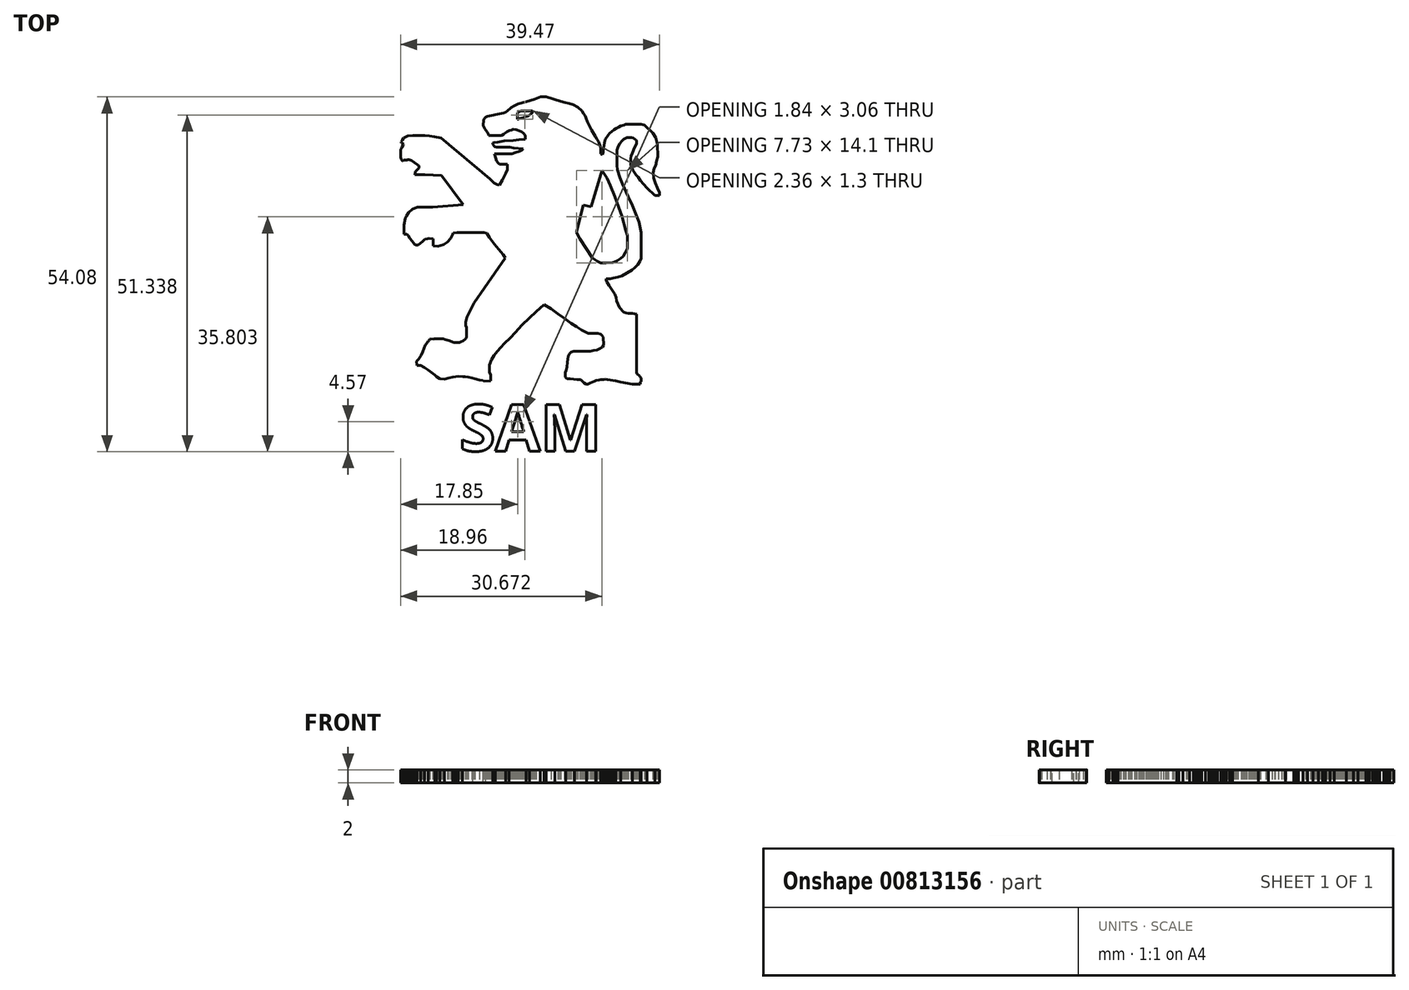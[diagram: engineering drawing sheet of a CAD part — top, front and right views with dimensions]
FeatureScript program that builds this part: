
annotation { "Feature Type Name" : "Feature", "Feature Type Description" : "" }
export const myFeature = defineFeature(function(context is Context, id is Id, definition is map)
    precondition{}
    {
        {
            var Q0;
            Q0=qCreatedBy(makeId("Top.planeOp"),FACE);
            var sketch = newSketch(context, id + "F0", { "sketchPlane" : qUnion([Q0])});
            skLineSegment(sketch, "E0", {"start": v(13.97, 0.9) * mm, "end": v(13.97, 1.77) * mm});
            skLineSegment(sketch, "E1", {"start": v(13.97, 1.77) * mm, "end": v(13.78, 2.26) * mm});
            skLineSegment(sketch, "E2", {"start": v(13.78, 2.26) * mm, "end": v(13.78, 3.3) * mm});
            skLineSegment(sketch, "E3", {"start": v(13.78, 3.3) * mm, "end": v(14.1, 4.13) * mm});
            skLineSegment(sketch, "E4", {"start": v(14.1, 4.13) * mm, "end": v(14.5, 4.8) * mm});
            skLineSegment(sketch, "E5", {"start": v(14.5, 4.8) * mm, "end": v(15, 5.39) * mm});
            skLineSegment(sketch, "E6", {"start": v(15, 5.39) * mm, "end": v(15.48, 5.98) * mm});
            skLineSegment(sketch, "E7", {"start": v(15.48, 5.98) * mm, "end": v(16.06, 6.6) * mm});
            skLineSegment(sketch, "E8", {"start": v(16.06, 6.6) * mm, "end": v(16.94, 7.44) * mm});
            skLineSegment(sketch, "E9", {"start": v(16.94, 7.44) * mm, "end": v(17.73, 8.26) * mm});
            skLineSegment(sketch, "E10", {"start": v(17.73, 8.26) * mm, "end": v(18.78, 9.4) * mm});
            skLineSegment(sketch, "E11", {"start": v(18.78, 9.4) * mm, "end": v(19.9, 10.48) * mm});
            skLineSegment(sketch, "E12", {"start": v(19.9, 10.48) * mm, "end": v(20.9, 11.46) * mm});
            skLineSegment(sketch, "E13", {"start": v(20.9, 11.46) * mm, "end": v(22.1, 12.53) * mm});
            skLineSegment(sketch, "E14", {"start": v(22.1, 12.53) * mm, "end": v(23.17, 11.89) * mm});
            skLineSegment(sketch, "E15", {"start": v(23.17, 11.89) * mm, "end": v(24.23, 11.11) * mm});
            skLineSegment(sketch, "E16", {"start": v(24.23, 11.11) * mm, "end": v(25.22, 10.45) * mm});
            skLineSegment(sketch, "E17", {"start": v(25.22, 10.45) * mm, "end": v(26.25, 9.7) * mm});
            skLineSegment(sketch, "E18", {"start": v(26.25, 9.7) * mm, "end": v(27.06, 9.18) * mm});
            skLineSegment(sketch, "E19", {"start": v(27.06, 9.18) * mm, "end": v(27.84, 8.67) * mm});
            skLineSegment(sketch, "E20", {"start": v(27.84, 8.67) * mm, "end": v(28.85, 8.16) * mm});
            skLineSegment(sketch, "E21", {"start": v(28.85, 8.16) * mm, "end": v(30.3, 8.16) * mm});
            skLineSegment(sketch, "E22", {"start": v(30.3, 8.16) * mm, "end": v(30.76, 8) * mm});
            skLineSegment(sketch, "E23", {"start": v(30.76, 8) * mm, "end": v(30.95, 7.82) * mm});
            skLineSegment(sketch, "E24", {"start": v(30.95, 7.82) * mm, "end": v(31.1, 7.55) * mm});
            skLineSegment(sketch, "E25", {"start": v(31.1, 7.55) * mm, "end": v(31.17, 6.37) * mm});
            skLineSegment(sketch, "E26", {"start": v(31.17, 6.37) * mm, "end": v(30.99, 6.03) * mm});
            skLineSegment(sketch, "E27", {"start": v(30.99, 6.03) * mm, "end": v(30.55, 5.77) * mm});
            skLineSegment(sketch, "E28", {"start": v(30.55, 5.77) * mm, "end": v(30.16, 5.62) * mm});
            skLineSegment(sketch, "E29", {"start": v(30.16, 5.62) * mm, "end": v(29.68, 5.5) * mm});
            skLineSegment(sketch, "E30", {"start": v(29.68, 5.5) * mm, "end": v(29.13, 5.42) * mm});
            skLineSegment(sketch, "E31", {"start": v(29.13, 5.42) * mm, "end": v(26.64, 5.42) * mm});
            skLineSegment(sketch, "E32", {"start": v(26.64, 5.42) * mm, "end": v(26.27, 5.28) * mm});
            skLineSegment(sketch, "E33", {"start": v(26.27, 5.28) * mm, "end": v(26, 5.01) * mm});
            skLineSegment(sketch, "E34", {"start": v(26, 5.01) * mm, "end": v(25.83, 4.63) * mm});
            skLineSegment(sketch, "E35", {"start": v(25.83, 4.63) * mm, "end": v(25.7, 3.74) * mm});
            skLineSegment(sketch, "E36", {"start": v(25.7, 3.74) * mm, "end": v(25.59, 3.02) * mm});
            skLineSegment(sketch, "E37", {"start": v(25.59, 3.02) * mm, "end": v(25.45, 2.5) * mm});
            skLineSegment(sketch, "E38", {"start": v(25.45, 2.5) * mm, "end": v(25.34, 2.18) * mm});
            skLineSegment(sketch, "E39", {"start": v(25.34, 2.18) * mm, "end": v(25.34, 1.47) * mm});
            skLineSegment(sketch, "E40", {"start": v(25.34, 1.47) * mm, "end": v(25.6, 1.23) * mm});
            skLineSegment(sketch, "E41", {"start": v(25.6, 1.23) * mm, "end": v(26.1, 1.23) * mm});
            skLineSegment(sketch, "E42", {"start": v(26.1, 1.23) * mm, "end": v(26.61, 1.15) * mm});
            skLineSegment(sketch, "E43", {"start": v(26.61, 1.15) * mm, "end": v(27.13, 1.07) * mm});
            skLineSegment(sketch, "E44", {"start": v(27.13, 1.07) * mm, "end": v(27.68, 1.07) * mm});
            skLineSegment(sketch, "E45", {"start": v(27.68, 1.07) * mm, "end": v(27.95, 0.82) * mm});
            skLineSegment(sketch, "E46", {"start": v(27.95, 0.82) * mm, "end": v(28.2, 0.58) * mm});
            skLineSegment(sketch, "E47", {"start": v(28.2, 0.58) * mm, "end": v(28.54, 0.4) * mm});
            skLineSegment(sketch, "E48", {"start": v(28.54, 0.4) * mm, "end": v(28.79, 0.4) * mm});
            skLineSegment(sketch, "E49", {"start": v(28.79, 0.4) * mm, "end": v(29.18, 0.58) * mm});
            skLineSegment(sketch, "E50", {"start": v(29.18, 0.58) * mm, "end": v(29.45, 0.7) * mm});
            skLineSegment(sketch, "E51", {"start": v(29.45, 0.7) * mm, "end": v(29.78, 0.82) * mm});
            skLineSegment(sketch, "E52", {"start": v(29.78, 0.82) * mm, "end": v(30.07, 0.95) * mm});
            skLineSegment(sketch, "E53", {"start": v(30.07, 0.95) * mm, "end": v(30.46, 1.03) * mm});
            skLineSegment(sketch, "E54", {"start": v(30.46, 1.03) * mm, "end": v(30.78, 1.1) * mm});
            skLineSegment(sketch, "E55", {"start": v(30.78, 1.1) * mm, "end": v(31.2, 1.1) * mm});
            skLineSegment(sketch, "E56", {"start": v(31.2, 1.1) * mm, "end": v(31.46, 1.15) * mm});
            skLineSegment(sketch, "E57", {"start": v(31.46, 1.15) * mm, "end": v(31.77, 1.08) * mm});
            skLineSegment(sketch, "E58", {"start": v(31.77, 1.08) * mm, "end": v(32.19, 1.02) * mm});
            skLineSegment(sketch, "E59", {"start": v(32.19, 1.02) * mm, "end": v(32.57, 0.95) * mm});
            skLineSegment(sketch, "E60", {"start": v(32.57, 0.95) * mm, "end": v(33.05, 0.88) * mm});
            skLineSegment(sketch, "E61", {"start": v(33.05, 0.88) * mm, "end": v(33.8, 0.71) * mm});
            skLineSegment(sketch, "E62", {"start": v(33.8, 0.71) * mm, "end": v(35.55, 0.37) * mm});
            skLineSegment(sketch, "E63", {"start": v(35.55, 0.37) * mm, "end": v(36.8, 0.37) * mm});
            skLineSegment(sketch, "E64", {"start": v(36.8, 0.37) * mm, "end": v(36.8, 0.75) * mm});
            skLineSegment(sketch, "E65", {"start": v(36.8, 0.75) * mm, "end": v(36.88, 0.75) * mm});
            skLineSegment(sketch, "E66", {"start": v(36.88, 0.75) * mm, "end": v(36.88, 1.34) * mm});
            skLineSegment(sketch, "E67", {"start": v(36.88, 1.34) * mm, "end": v(36.7, 1.52) * mm});
            skLineSegment(sketch, "E68", {"start": v(36.7, 1.52) * mm, "end": v(36.66, 1.64) * mm});
            skLineSegment(sketch, "E69", {"start": v(36.66, 1.64) * mm, "end": v(36.28, 2) * mm});
            skLineSegment(sketch, "E70", {"start": v(36.28, 2) * mm, "end": v(36.22, 2.16) * mm});
            skLineSegment(sketch, "E71", {"start": v(36.22, 2.16) * mm, "end": v(36.22, 11.05) * mm});
            skLineSegment(sketch, "E72", {"start": v(36.22, 11.05) * mm, "end": v(35.57, 11.18) * mm});
            skLineSegment(sketch, "E73", {"start": v(35.57, 11.18) * mm, "end": v(34.95, 11.18) * mm});
            skLineSegment(sketch, "E74", {"start": v(34.95, 11.18) * mm, "end": v(34.6, 11.25) * mm});
            skLineSegment(sketch, "E75", {"start": v(34.6, 11.25) * mm, "end": v(34.26, 11.4) * mm});
            skLineSegment(sketch, "E76", {"start": v(34.26, 11.4) * mm, "end": v(33.93, 11.72) * mm});
            skLineSegment(sketch, "E77", {"start": v(33.93, 11.72) * mm, "end": v(33.59, 12.05) * mm});
            skLineSegment(sketch, "E78", {"start": v(33.59, 12.05) * mm, "end": v(33.4, 12.53) * mm});
            skLineSegment(sketch, "E79", {"start": v(33.4, 12.53) * mm, "end": v(33.2, 13.07) * mm});
            skLineSegment(sketch, "E80", {"start": v(33.2, 13.07) * mm, "end": v(33.07, 13.59) * mm});
            skLineSegment(sketch, "E81", {"start": v(33.07, 13.59) * mm, "end": v(32.88, 14.08) * mm});
            skLineSegment(sketch, "E82", {"start": v(32.88, 14.08) * mm, "end": v(32.65, 14.48) * mm});
            skLineSegment(sketch, "E83", {"start": v(32.65, 14.48) * mm, "end": v(32.38, 14.9) * mm});
            skLineSegment(sketch, "E84", {"start": v(32.38, 14.9) * mm, "end": v(32, 15.46) * mm});
            skLineSegment(sketch, "E85", {"start": v(32, 15.46) * mm, "end": v(31.7, 15.95) * mm});
            skLineSegment(sketch, "E86", {"start": v(31.7, 15.95) * mm, "end": v(31.56, 16.28) * mm});
            skLineSegment(sketch, "E87", {"start": v(31.56, 16.28) * mm, "end": v(31.6, 16.45) * mm});
            skLineSegment(sketch, "E88", {"start": v(31.6, 16.45) * mm, "end": v(32.18, 16.45) * mm});
            skLineSegment(sketch, "E89", {"start": v(32.18, 16.45) * mm, "end": v(32.7, 16.57) * mm});
            skLineSegment(sketch, "E90", {"start": v(32.7, 16.57) * mm, "end": v(33.34, 16.74) * mm});
            skLineSegment(sketch, "E91", {"start": v(33.34, 16.74) * mm, "end": v(33.96, 16.92) * mm});
            skLineSegment(sketch, "E92", {"start": v(33.96, 16.92) * mm, "end": v(34.77, 17.32) * mm});
            skLineSegment(sketch, "E93", {"start": v(34.77, 17.32) * mm, "end": v(35.5, 17.8) * mm});
            skLineSegment(sketch, "E94", {"start": v(35.5, 17.8) * mm, "end": v(35.97, 18.18) * mm});
            skLineSegment(sketch, "E95", {"start": v(35.97, 18.18) * mm, "end": v(36.4, 18.63) * mm});
            skLineSegment(sketch, "E96", {"start": v(36.4, 18.63) * mm, "end": v(36.73, 19.12) * mm});
            skLineSegment(sketch, "E97", {"start": v(36.73, 19.12) * mm, "end": v(36.88, 19.57) * mm});
            skLineSegment(sketch, "E98", {"start": v(36.88, 19.57) * mm, "end": v(36.88, 23.54) * mm});
            skLineSegment(sketch, "E99", {"start": v(36.88, 23.54) * mm, "end": v(36.56, 25.08) * mm});
            skPoint(sketch, "E99.endSnap0", {"position": v(36.56, 18.87) * mm});
            skLineSegment(sketch, "E100", {"start": v(36.56, 25.08) * mm, "end": v(36.04, 26.42) * mm});
            skLineSegment(sketch, "E101", {"start": v(36.04, 26.42) * mm, "end": v(35.56, 27.66) * mm});
            skLineSegment(sketch, "E102", {"start": v(35.56, 27.66) * mm, "end": v(34.95, 28.94) * mm});
            skLineSegment(sketch, "E103", {"start": v(34.95, 28.94) * mm, "end": v(34.56, 29.8) * mm});
            skLineSegment(sketch, "E104", {"start": v(34.56, 29.8) * mm, "end": v(34.05, 30.91) * mm});
            skLineSegment(sketch, "E105", {"start": v(34.05, 30.91) * mm, "end": v(33.67, 31.9) * mm});
            skLineSegment(sketch, "E106", {"start": v(33.67, 31.9) * mm, "end": v(33.32, 33.1) * mm});
            skLineSegment(sketch, "E107", {"start": v(33.32, 33.1) * mm, "end": v(33.23, 33.72) * mm});
            skLineSegment(sketch, "E108", {"start": v(33.23, 33.72) * mm, "end": v(33.23, 36.07) * mm});
            skLineSegment(sketch, "E109", {"start": v(33.23, 36.07) * mm, "end": v(33.42, 36.63) * mm});
            skLineSegment(sketch, "E110", {"start": v(33.42, 36.63) * mm, "end": v(33.67, 37.12) * mm});
            skLineSegment(sketch, "E111", {"start": v(33.67, 37.12) * mm, "end": v(33.96, 37.49) * mm});
            skLineSegment(sketch, "E112", {"start": v(33.96, 37.49) * mm, "end": v(34.22, 37.75) * mm});
            skLineSegment(sketch, "E113", {"start": v(34.22, 37.75) * mm, "end": v(34.47, 37.87) * mm});
            skLineSegment(sketch, "E114", {"start": v(34.47, 37.87) * mm, "end": v(34.73, 37.98) * mm});
            skLineSegment(sketch, "E115", {"start": v(34.73, 37.98) * mm, "end": v(35.44, 37.98) * mm});
            skLineSegment(sketch, "E116", {"start": v(35.44, 37.98) * mm, "end": v(35.7, 37.9) * mm});
            skLineSegment(sketch, "E117", {"start": v(35.7, 37.9) * mm, "end": v(35.97, 37.76) * mm});
            skLineSegment(sketch, "E118", {"start": v(35.97, 37.76) * mm, "end": v(36.12, 37.6) * mm});
            skLineSegment(sketch, "E119", {"start": v(36.12, 37.6) * mm, "end": v(36.22, 37.46) * mm});
            skLineSegment(sketch, "E120", {"start": v(36.22, 37.46) * mm, "end": v(36.22, 37.03) * mm});
            skLineSegment(sketch, "E121", {"start": v(36.22, 37.03) * mm, "end": v(36.1, 36.8) * mm});
            skLineSegment(sketch, "E122", {"start": v(36.1, 36.8) * mm, "end": v(35.92, 36.44) * mm});
            skLineSegment(sketch, "E123", {"start": v(35.92, 36.44) * mm, "end": v(35.55, 35.66) * mm});
            skLineSegment(sketch, "E124", {"start": v(35.55, 35.66) * mm, "end": v(35.4, 35.18) * mm});
            skLineSegment(sketch, "E125", {"start": v(35.4, 35.18) * mm, "end": v(35.32, 34.8) * mm});
            skLineSegment(sketch, "E126", {"start": v(35.32, 34.8) * mm, "end": v(35.32, 33.86) * mm});
            skLineSegment(sketch, "E127", {"start": v(35.32, 33.86) * mm, "end": v(35.45, 33.51) * mm});
            skLineSegment(sketch, "E128", {"start": v(35.45, 33.51) * mm, "end": v(35.66, 33.06) * mm});
            skLineSegment(sketch, "E129", {"start": v(35.66, 33.06) * mm, "end": v(35.9, 32.68) * mm});
            skLineSegment(sketch, "E130", {"start": v(35.9, 32.68) * mm, "end": v(36.17, 32.25) * mm});
            skLineSegment(sketch, "E131", {"start": v(36.17, 32.25) * mm, "end": v(36.45, 31.93) * mm});
            skLineSegment(sketch, "E132", {"start": v(36.45, 31.93) * mm, "end": v(36.79, 31.47) * mm});
            skLineSegment(sketch, "E133", {"start": v(36.79, 31.47) * mm, "end": v(37.29, 30.9) * mm});
            skLineSegment(sketch, "E134", {"start": v(37.29, 30.9) * mm, "end": v(37.8, 30.3) * mm});
            skLineSegment(sketch, "E135", {"start": v(37.8, 30.3) * mm, "end": v(38.48, 29.64) * mm});
            skLineSegment(sketch, "E136", {"start": v(38.48, 29.64) * mm, "end": v(38.98, 29.16) * mm});
            skLineSegment(sketch, "E137", {"start": v(38.98, 29.16) * mm, "end": v(39.73, 29.16) * mm});
            skLineSegment(sketch, "E138", {"start": v(39.73, 29.16) * mm, "end": v(39.73, 29.6) * mm});
            skLineSegment(sketch, "E139", {"start": v(39.73, 29.6) * mm, "end": v(39.38, 30.31) * mm});
            skLineSegment(sketch, "E140", {"start": v(39.38, 30.31) * mm, "end": v(39.09, 31.04) * mm});
            skLineSegment(sketch, "E141", {"start": v(39.09, 31.04) * mm, "end": v(38.84, 31.82) * mm});
            skLineSegment(sketch, "E142", {"start": v(38.84, 31.82) * mm, "end": v(38.78, 32.67) * mm});
            skLineSegment(sketch, "E143", {"start": v(38.78, 32.67) * mm, "end": v(38.9, 33.28) * mm});
            skLineSegment(sketch, "E144", {"start": v(38.9, 33.28) * mm, "end": v(39.14, 33.76) * mm});
            skLineSegment(sketch, "E145", {"start": v(39.14, 33.76) * mm, "end": v(39.27, 34.44) * mm});
            skLineSegment(sketch, "E146", {"start": v(39.27, 34.44) * mm, "end": v(39.45, 35.1) * mm});
            skLineSegment(sketch, "E147", {"start": v(39.45, 35.1) * mm, "end": v(39.36, 36.94) * mm});
            skPoint(sketch, "E147.endSnap0", {"position": v(39.36, 34.76) * mm});
            skLineSegment(sketch, "E148", {"start": v(39.36, 36.94) * mm, "end": v(39.14, 37.98) * mm});
            skLineSegment(sketch, "E149", {"start": v(39.14, 37.98) * mm, "end": v(38.7, 38.68) * mm});
            skLineSegment(sketch, "E150", {"start": v(38.7, 38.68) * mm, "end": v(37.8, 39.55) * mm});
            skLineSegment(sketch, "E151", {"start": v(37.8, 39.55) * mm, "end": v(37.42, 39.9) * mm});
            skLineSegment(sketch, "E152", {"start": v(37.42, 39.9) * mm, "end": v(36.88, 40.01) * mm});
            skLineSegment(sketch, "E153", {"start": v(36.88, 40.01) * mm, "end": v(34.56, 40.01) * mm});
            skLineSegment(sketch, "E154", {"start": v(34.56, 40.01) * mm, "end": v(34.3, 39.9) * mm});
            skLineSegment(sketch, "E155", {"start": v(34.3, 39.9) * mm, "end": v(33.8, 39.79) * mm});
            skLineSegment(sketch, "E156", {"start": v(33.8, 39.79) * mm, "end": v(33.48, 39.6) * mm});
            skLineSegment(sketch, "E157", {"start": v(33.48, 39.6) * mm, "end": v(33.12, 39.4) * mm});
            skLineSegment(sketch, "E158", {"start": v(33.12, 39.4) * mm, "end": v(32.8, 39.19) * mm});
            skLineSegment(sketch, "E159", {"start": v(32.8, 39.19) * mm, "end": v(32.5, 38.95) * mm});
            skLineSegment(sketch, "E160", {"start": v(32.5, 38.95) * mm, "end": v(32.1, 38.6) * mm});
            skLineSegment(sketch, "E161", {"start": v(32.1, 38.6) * mm, "end": v(31.9, 38.35) * mm});
            skLineSegment(sketch, "E162", {"start": v(31.9, 38.35) * mm, "end": v(31.72, 38.09) * mm});
            skLineSegment(sketch, "E163", {"start": v(31.72, 38.09) * mm, "end": v(31.47, 37.7) * mm});
            skLineSegment(sketch, "E164", {"start": v(31.47, 37.7) * mm, "end": v(31.34, 37.23) * mm});
            skLineSegment(sketch, "E165", {"start": v(31.34, 37.23) * mm, "end": v(31.25, 36.8) * mm});
            skLineSegment(sketch, "E166", {"start": v(31.25, 36.8) * mm, "end": v(31.18, 36.42) * mm});
            skLineSegment(sketch, "E167", {"start": v(31.18, 36.42) * mm, "end": v(31.12, 35.86) * mm});
            skLineSegment(sketch, "E168", {"start": v(31.12, 35.86) * mm, "end": v(31.05, 35.5) * mm});
            skLineSegment(sketch, "E169", {"start": v(31.05, 35.5) * mm, "end": v(31, 35.38) * mm});
            skLineSegment(sketch, "E170", {"start": v(31, 35.38) * mm, "end": v(30.77, 35.53) * mm});
            skLineSegment(sketch, "E171", {"start": v(30.77, 35.53) * mm, "end": v(30.77, 36.26) * mm});
            skLineSegment(sketch, "E172", {"start": v(30.77, 36.26) * mm, "end": v(30.66, 36.66) * mm});
            skLineSegment(sketch, "E173", {"start": v(30.66, 36.66) * mm, "end": v(30.4, 37.32) * mm});
            skLineSegment(sketch, "E174", {"start": v(30.4, 37.32) * mm, "end": v(30.16, 37.7) * mm});
            skLineSegment(sketch, "E175", {"start": v(30.16, 37.7) * mm, "end": v(29.9, 38.19) * mm});
            skLineSegment(sketch, "E176", {"start": v(29.9, 38.19) * mm, "end": v(29.57, 38.72) * mm});
            skLineSegment(sketch, "E177", {"start": v(29.57, 38.72) * mm, "end": v(29.32, 39.1) * mm});
            skLineSegment(sketch, "E178", {"start": v(29.32, 39.1) * mm, "end": v(29.15, 39.48) * mm});
            skLineSegment(sketch, "E179", {"start": v(29.15, 39.48) * mm, "end": v(28.93, 39.97) * mm});
            skLineSegment(sketch, "E180", {"start": v(28.93, 39.97) * mm, "end": v(28.72, 40.42) * mm});
            skLineSegment(sketch, "E181", {"start": v(28.72, 40.42) * mm, "end": v(28.54, 40.9) * mm});
            skLineSegment(sketch, "E182", {"start": v(28.54, 40.9) * mm, "end": v(28.38, 41.3) * mm});
            skLineSegment(sketch, "E183", {"start": v(28.38, 41.3) * mm, "end": v(28.17, 41.6) * mm});
            skLineSegment(sketch, "E184", {"start": v(28.17, 41.6) * mm, "end": v(27.9, 42.03) * mm});
            skLineSegment(sketch, "E185", {"start": v(27.9, 42.03) * mm, "end": v(27.28, 42.62) * mm});
            skLineSegment(sketch, "E186", {"start": v(27.28, 42.62) * mm, "end": v(26.96, 42.78) * mm});
            skLineSegment(sketch, "E187", {"start": v(26.96, 42.78) * mm, "end": v(26.57, 42.98) * mm});
            skLineSegment(sketch, "E188", {"start": v(26.57, 42.98) * mm, "end": v(25.92, 43.2) * mm});
            skLineSegment(sketch, "E189", {"start": v(25.92, 43.2) * mm, "end": v(25.34, 43.32) * mm});
            skLineSegment(sketch, "E190", {"start": v(25.34, 43.32) * mm, "end": v(24.65, 43.5) * mm});
            skLineSegment(sketch, "E191", {"start": v(24.65, 43.5) * mm, "end": v(22.4, 44.18) * mm});
            skLineSegment(sketch, "E192", {"start": v(22.4, 44.18) * mm, "end": v(21.62, 44.18) * mm});
            skLineSegment(sketch, "E193", {"start": v(21.62, 44.18) * mm, "end": v(20.63, 43.8) * mm});
            skLineSegment(sketch, "E194", {"start": v(20.63, 43.8) * mm, "end": v(19.41, 43.47) * mm});
            skLineSegment(sketch, "E195", {"start": v(19.41, 43.47) * mm, "end": v(18.2, 43.12) * mm});
            skLineSegment(sketch, "E196", {"start": v(18.2, 43.12) * mm, "end": v(17.53, 42.81) * mm});
            skLineSegment(sketch, "E197", {"start": v(17.53, 42.81) * mm, "end": v(17.1, 42.55) * mm});
            skLineSegment(sketch, "E198", {"start": v(17.1, 42.55) * mm, "end": v(16.76, 42.25) * mm});
            skLineSegment(sketch, "E199", {"start": v(16.76, 42.25) * mm, "end": v(16.47, 42) * mm});
            skLineSegment(sketch, "E200", {"start": v(16.47, 42) * mm, "end": v(16.3, 41.88) * mm});
            skLineSegment(sketch, "E201", {"start": v(16.3, 41.88) * mm, "end": v(15.98, 41.76) * mm});
            skLineSegment(sketch, "E202", {"start": v(15.98, 41.76) * mm, "end": v(15.63, 41.67) * mm});
            skLineSegment(sketch, "E203", {"start": v(15.63, 41.67) * mm, "end": v(13.48, 41.23) * mm});
            skLineSegment(sketch, "E204", {"start": v(13.48, 41.23) * mm, "end": v(13.22, 41.1) * mm});
            skLineSegment(sketch, "E205", {"start": v(13.22, 41.1) * mm, "end": v(13.02, 40.88) * mm});
            skLineSegment(sketch, "E206", {"start": v(13.02, 40.88) * mm, "end": v(12.91, 40.67) * mm});
            skLineSegment(sketch, "E207", {"start": v(12.91, 40.67) * mm, "end": v(12.86, 39.83) * mm});
            skLineSegment(sketch, "E208", {"start": v(12.86, 39.83) * mm, "end": v(12.97, 39.58) * mm});
            skLineSegment(sketch, "E209", {"start": v(12.97, 39.58) * mm, "end": v(13.08, 39.35) * mm});
            skLineSegment(sketch, "E210", {"start": v(13.08, 39.35) * mm, "end": v(13.24, 39.13) * mm});
            skLineSegment(sketch, "E211", {"start": v(13.24, 39.13) * mm, "end": v(13.45, 38.8) * mm});
            skLineSegment(sketch, "E212", {"start": v(13.45, 38.8) * mm, "end": v(13.57, 38.58) * mm});
            skLineSegment(sketch, "E213", {"start": v(13.57, 38.58) * mm, "end": v(13.64, 38.44) * mm});
            skLineSegment(sketch, "E214", {"start": v(13.64, 38.44) * mm, "end": v(13.65, 38.3) * mm});
            skLineSegment(sketch, "E215", {"start": v(13.65, 38.3) * mm, "end": v(15.66, 38.3) * mm});
            skLineSegment(sketch, "E216", {"start": v(15.66, 38.3) * mm, "end": v(15.98, 38.51) * mm});
            skLineSegment(sketch, "E217", {"start": v(15.98, 38.51) * mm, "end": v(16.24, 38.74) * mm});
            skLineSegment(sketch, "E218", {"start": v(16.24, 38.74) * mm, "end": v(16.48, 38.9) * mm});
            skLineSegment(sketch, "E219", {"start": v(16.48, 38.9) * mm, "end": v(16.82, 39.04) * mm});
            skLineSegment(sketch, "E220", {"start": v(16.82, 39.04) * mm, "end": v(17.13, 39.13) * mm});
            skLineSegment(sketch, "E221", {"start": v(17.13, 39.13) * mm, "end": v(17.43, 39.23) * mm});
            skLineSegment(sketch, "E222", {"start": v(17.43, 39.23) * mm, "end": v(17.87, 39.22) * mm});
            skLineSegment(sketch, "E223", {"start": v(17.87, 39.22) * mm, "end": v(18.02, 39.14) * mm});
            skLineSegment(sketch, "E224", {"start": v(18.02, 39.14) * mm, "end": v(18.4, 39) * mm});
            skLineSegment(sketch, "E225", {"start": v(18.4, 39) * mm, "end": v(18.7, 38.85) * mm});
            skLineSegment(sketch, "E226", {"start": v(18.7, 38.85) * mm, "end": v(18.96, 38.68) * mm});
            skLineSegment(sketch, "E227", {"start": v(18.96, 38.68) * mm, "end": v(19.14, 38.5) * mm});
            skLineSegment(sketch, "E228", {"start": v(19.14, 38.5) * mm, "end": v(19.27, 38.26) * mm});
            skLineSegment(sketch, "E229", {"start": v(19.27, 38.26) * mm, "end": v(19.27, 37.76) * mm});
            skLineSegment(sketch, "E230", {"start": v(19.27, 37.76) * mm, "end": v(18.84, 37.72) * mm});
            skLineSegment(sketch, "E231", {"start": v(18.84, 37.72) * mm, "end": v(18.3, 37.68) * mm});
            skLineSegment(sketch, "E232", {"start": v(18.3, 37.68) * mm, "end": v(17.43, 37.56) * mm});
            skLineSegment(sketch, "E233", {"start": v(17.43, 37.56) * mm, "end": v(16.67, 37.5) * mm});
            skLineSegment(sketch, "E234", {"start": v(16.67, 37.5) * mm, "end": v(16.04, 37.45) * mm});
            skLineSegment(sketch, "E235", {"start": v(16.04, 37.45) * mm, "end": v(15.05, 37.3) * mm});
            skLineSegment(sketch, "E236", {"start": v(15.05, 37.3) * mm, "end": v(14.49, 37.25) * mm});
            skLineSegment(sketch, "E237", {"start": v(14.49, 37.25) * mm, "end": v(14.33, 37.13) * mm});
            skLineSegment(sketch, "E238", {"start": v(14.33, 37.13) * mm, "end": v(14.29, 36.94) * mm});
            skLineSegment(sketch, "E239", {"start": v(14.29, 36.94) * mm, "end": v(14.46, 36.75) * mm});
            skLineSegment(sketch, "E240", {"start": v(14.46, 36.75) * mm, "end": v(14.62, 36.6) * mm});
            skLineSegment(sketch, "E241", {"start": v(14.62, 36.6) * mm, "end": v(14.87, 36.53) * mm});
            skLineSegment(sketch, "E242", {"start": v(14.87, 36.53) * mm, "end": v(16.4, 36.53) * mm});
            skLineSegment(sketch, "E243", {"start": v(16.4, 36.53) * mm, "end": v(16.89, 36.5) * mm});
            skLineSegment(sketch, "E244", {"start": v(16.89, 36.5) * mm, "end": v(17.48, 36.39) * mm});
            skLineSegment(sketch, "E245", {"start": v(17.48, 36.39) * mm, "end": v(18.2, 36.34) * mm});
            skLineSegment(sketch, "E246", {"start": v(18.2, 36.34) * mm, "end": v(18.92, 36.3) * mm});
            skLineSegment(sketch, "E247", {"start": v(18.92, 36.3) * mm, "end": v(18.76, 36.09) * mm});
            skLineSegment(sketch, "E248", {"start": v(18.76, 36.09) * mm, "end": v(18.34, 35.87) * mm});
            skLineSegment(sketch, "E249", {"start": v(18.34, 35.87) * mm, "end": v(17.75, 35.68) * mm});
            skLineSegment(sketch, "E250", {"start": v(17.75, 35.68) * mm, "end": v(17.22, 35.54) * mm});
            skLineSegment(sketch, "E251", {"start": v(17.22, 35.54) * mm, "end": v(14.55, 35.54) * mm});
            skLineSegment(sketch, "E252", {"start": v(14.55, 35.54) * mm, "end": v(14.62, 35.26) * mm});
            skLineSegment(sketch, "E253", {"start": v(14.62, 35.26) * mm, "end": v(14.72, 34.87) * mm});
            skLineSegment(sketch, "E254", {"start": v(14.72, 34.87) * mm, "end": v(14.9, 34.44) * mm});
            skLineSegment(sketch, "E255", {"start": v(14.9, 34.44) * mm, "end": v(15.11, 34.14) * mm});
            skLineSegment(sketch, "E256", {"start": v(15.11, 34.14) * mm, "end": v(15.32, 33.94) * mm});
            skLineSegment(sketch, "E257", {"start": v(15.32, 33.94) * mm, "end": v(16.53, 33.94) * mm});
            skLineSegment(sketch, "E258", {"start": v(16.53, 33.94) * mm, "end": v(16.53, 33.1) * mm});
            skLineSegment(sketch, "E259", {"start": v(16.53, 33.1) * mm, "end": v(16.3, 32.52) * mm});
            skLineSegment(sketch, "E260", {"start": v(16.3, 32.52) * mm, "end": v(16.02, 31.98) * mm});
            skLineSegment(sketch, "E261", {"start": v(16.02, 31.98) * mm, "end": v(15.76, 31.48) * mm});
            skLineSegment(sketch, "E262", {"start": v(15.76, 31.48) * mm, "end": v(15.52, 31.11) * mm});
            skLineSegment(sketch, "E263", {"start": v(15.52, 31.11) * mm, "end": v(15.3, 30.77) * mm});
            skLineSegment(sketch, "E264", {"start": v(15.3, 30.77) * mm, "end": v(14.98, 30.79) * mm});
            skLineSegment(sketch, "E265", {"start": v(14.98, 30.79) * mm, "end": v(14.5, 31.04) * mm});
            skLineSegment(sketch, "E266", {"start": v(14.5, 31.04) * mm, "end": v(13.83, 31.68) * mm});
            skLineSegment(sketch, "E267", {"start": v(13.83, 31.68) * mm, "end": v(6.41, 37.9) * mm});
            skLineSegment(sketch, "E268", {"start": v(6.41, 37.9) * mm, "end": v(5.42, 38.11) * mm});
            skLineSegment(sketch, "E269", {"start": v(5.42, 38.11) * mm, "end": v(4.63, 38.26) * mm});
            skLineSegment(sketch, "E270", {"start": v(4.63, 38.26) * mm, "end": v(3.96, 38.3) * mm});
            skLineSegment(sketch, "E271", {"start": v(3.96, 38.3) * mm, "end": v(2.12, 38.3) * mm});
            skLineSegment(sketch, "E272", {"start": v(2.12, 38.3) * mm, "end": v(1.38, 38.25) * mm});
            skLineSegment(sketch, "E273", {"start": v(1.38, 38.25) * mm, "end": v(0.98, 38.03) * mm});
            skLineSegment(sketch, "E274", {"start": v(0.98, 38.03) * mm, "end": v(0.7, 37.9) * mm});
            skLineSegment(sketch, "E275", {"start": v(0.7, 37.9) * mm, "end": v(0.55, 37.61) * mm});
            skLineSegment(sketch, "E276", {"start": v(0.55, 37.61) * mm, "end": v(0.36, 37.33) * mm});
            skLineSegment(sketch, "E277", {"start": v(0.36, 37.33) * mm, "end": v(0.41, 37.13) * mm});
            skLineSegment(sketch, "E278", {"start": v(0.41, 37.13) * mm, "end": v(0.56, 37.1) * mm});
            skLineSegment(sketch, "E279", {"start": v(0.56, 37.1) * mm, "end": v(0.65, 37.04) * mm});
            skLineSegment(sketch, "E280", {"start": v(0.65, 37.04) * mm, "end": v(0.7, 36.94) * mm});
            skLineSegment(sketch, "E281", {"start": v(0.7, 36.94) * mm, "end": v(0.65, 36.87) * mm});
            skLineSegment(sketch, "E282", {"start": v(0.65, 36.87) * mm, "end": v(0.57, 36.71) * mm});
            skLineSegment(sketch, "E283", {"start": v(0.57, 36.71) * mm, "end": v(0.48, 36.53) * mm});
            skLineSegment(sketch, "E284", {"start": v(0.48, 36.53) * mm, "end": v(0.4, 36.4) * mm});
            skLineSegment(sketch, "E285", {"start": v(0.4, 36.4) * mm, "end": v(0.33, 36.28) * mm});
            skLineSegment(sketch, "E286", {"start": v(0.33, 36.28) * mm, "end": v(0.26, 36.18) * mm});
            skLineSegment(sketch, "E287", {"start": v(0.26, 36.18) * mm, "end": v(0.26, 34.92) * mm});
            skLineSegment(sketch, "E288", {"start": v(0.26, 34.92) * mm, "end": v(0.34, 34.84) * mm});
            skLineSegment(sketch, "E289", {"start": v(0.34, 34.84) * mm, "end": v(0.34, 34.65) * mm});
            skLineSegment(sketch, "E290", {"start": v(0.34, 34.65) * mm, "end": v(0.43, 34.6) * mm});
            skLineSegment(sketch, "E291", {"start": v(0.43, 34.6) * mm, "end": v(0.5, 34.44) * mm});
            skLineSegment(sketch, "E292", {"start": v(0.5, 34.44) * mm, "end": v(0.57, 34.43) * mm});
            skLineSegment(sketch, "E293", {"start": v(0.57, 34.43) * mm, "end": v(0.7, 34.56) * mm});
            skLineSegment(sketch, "E294", {"start": v(0.7, 34.56) * mm, "end": v(1.24, 34.56) * mm});
            skLineSegment(sketch, "E295", {"start": v(1.24, 34.56) * mm, "end": v(1.36, 34.63) * mm});
            skLineSegment(sketch, "E296", {"start": v(1.36, 34.63) * mm, "end": v(1.55, 34.61) * mm});
            skLineSegment(sketch, "E297", {"start": v(1.55, 34.61) * mm, "end": v(1.93, 34.46) * mm});
            skLineSegment(sketch, "E298", {"start": v(1.93, 34.46) * mm, "end": v(2.83, 33.87) * mm});
            skLineSegment(sketch, "E299", {"start": v(2.83, 33.87) * mm, "end": v(3, 33.7) * mm});
            skLineSegment(sketch, "E300", {"start": v(3, 33.7) * mm, "end": v(3.06, 33.54) * mm});
            skLineSegment(sketch, "E301", {"start": v(3.06, 33.54) * mm, "end": v(3.04, 33.37) * mm});
            skLineSegment(sketch, "E302", {"start": v(3.04, 33.37) * mm, "end": v(2.54, 32.86) * mm});
            skLineSegment(sketch, "E303", {"start": v(2.54, 32.86) * mm, "end": v(2.47, 32.7) * mm});
            skLineSegment(sketch, "E304", {"start": v(2.47, 32.7) * mm, "end": v(2.44, 32.35) * mm});
            skLineSegment(sketch, "E305", {"start": v(2.44, 32.35) * mm, "end": v(3.97, 32.32) * mm});
            skLineSegment(sketch, "E306", {"start": v(3.97, 32.32) * mm, "end": v(6.47, 32.2) * mm});
            skLineSegment(sketch, "E307", {"start": v(6.47, 32.2) * mm, "end": v(9.76, 27.76) * mm});
            skLineSegment(sketch, "E308", {"start": v(9.76, 27.76) * mm, "end": v(8.12, 27.63) * mm});
            skLineSegment(sketch, "E309", {"start": v(8.12, 27.63) * mm, "end": v(6.62, 27.51) * mm});
            skLineSegment(sketch, "E310", {"start": v(6.62, 27.51) * mm, "end": v(5.16, 27.4) * mm});
            skLineSegment(sketch, "E311", {"start": v(5.16, 27.4) * mm, "end": v(2.8, 27.4) * mm});
            skLineSegment(sketch, "E312", {"start": v(2.8, 27.4) * mm, "end": v(2.04, 27.05) * mm});
            skLineSegment(sketch, "E313", {"start": v(2.04, 27.05) * mm, "end": v(1.5, 26.58) * mm});
            skLineSegment(sketch, "E314", {"start": v(1.5, 26.58) * mm, "end": v(1.15, 26.07) * mm});
            skLineSegment(sketch, "E315", {"start": v(1.15, 26.07) * mm, "end": v(0.98, 25.65) * mm});
            skLineSegment(sketch, "E316", {"start": v(0.98, 25.65) * mm, "end": v(0.9, 25.22) * mm});
            skLineSegment(sketch, "E317", {"start": v(0.9, 25.22) * mm, "end": v(0.78, 24.64) * mm});
            skLineSegment(sketch, "E318", {"start": v(0.78, 24.64) * mm, "end": v(0.78, 23.26) * mm});
            skLineSegment(sketch, "E319", {"start": v(0.78, 23.26) * mm, "end": v(1.2, 23.26) * mm});
            skLineSegment(sketch, "E320", {"start": v(1.2, 23.26) * mm, "end": v(1.4, 23.05) * mm});
            skLineSegment(sketch, "E321", {"start": v(1.4, 23.05) * mm, "end": v(1.67, 22.63) * mm});
            skLineSegment(sketch, "E322", {"start": v(1.67, 22.63) * mm, "end": v(2.03, 22.14) * mm});
            skLineSegment(sketch, "E323", {"start": v(2.03, 22.14) * mm, "end": v(2.34, 21.7) * mm});
            skLineSegment(sketch, "E324", {"start": v(2.34, 21.7) * mm, "end": v(2.6, 21.62) * mm});
            skLineSegment(sketch, "E325", {"start": v(2.6, 21.62) * mm, "end": v(2.96, 21.6) * mm});
            skLineSegment(sketch, "E326", {"start": v(2.96, 21.6) * mm, "end": v(3.62, 22.2) * mm});
            skLineSegment(sketch, "E327", {"start": v(3.62, 22.2) * mm, "end": v(3.95, 22.47) * mm});
            skLineSegment(sketch, "E328", {"start": v(3.95, 22.47) * mm, "end": v(4.33, 22.58) * mm});
            skLineSegment(sketch, "E329", {"start": v(4.33, 22.58) * mm, "end": v(4.6, 22.61) * mm});
            skLineSegment(sketch, "E330", {"start": v(4.6, 22.61) * mm, "end": v(5.22, 22.57) * mm});
            skLineSegment(sketch, "E331", {"start": v(5.22, 22.57) * mm, "end": v(5.23, 21.45) * mm});
            skLineSegment(sketch, "E332", {"start": v(5.23, 21.45) * mm, "end": v(5.9, 21.41) * mm});
            skLineSegment(sketch, "E333", {"start": v(5.9, 21.41) * mm, "end": v(6.82, 21.65) * mm});
            skLineSegment(sketch, "E334", {"start": v(6.82, 21.65) * mm, "end": v(7.39, 22.08) * mm});
            skLineSegment(sketch, "E335", {"start": v(7.39, 22.08) * mm, "end": v(7.9, 22.6) * mm});
            skLineSegment(sketch, "E336", {"start": v(7.9, 22.6) * mm, "end": v(8.23, 23.26) * mm});
            skLineSegment(sketch, "E337", {"start": v(8.23, 23.26) * mm, "end": v(8.28, 23.45) * mm});
            skLineSegment(sketch, "E338", {"start": v(8.28, 23.45) * mm, "end": v(8.82, 23.49) * mm});
            skLineSegment(sketch, "E339", {"start": v(8.82, 23.49) * mm, "end": v(12.97, 23.49) * mm});
            skLineSegment(sketch, "E340", {"start": v(12.97, 23.49) * mm, "end": v(13.4, 23.37) * mm});
            skLineSegment(sketch, "E341", {"start": v(13.4, 23.37) * mm, "end": v(13.8, 22.74) * mm});
            skLineSegment(sketch, "E342", {"start": v(13.8, 22.74) * mm, "end": v(14.55, 21.74) * mm});
            skLineSegment(sketch, "E343", {"start": v(14.55, 21.74) * mm, "end": v(15.2, 20.98) * mm});
            skLineSegment(sketch, "E344", {"start": v(15.2, 20.98) * mm, "end": v(15.9, 20.12) * mm});
            skLineSegment(sketch, "E345", {"start": v(15.9, 20.12) * mm, "end": v(16.22, 19.61) * mm});
            skLineSegment(sketch, "E346", {"start": v(16.22, 19.61) * mm, "end": v(11.47, 12.76) * mm});
            skLineSegment(sketch, "E347", {"start": v(11.47, 12.76) * mm, "end": v(10.96, 11.76) * mm});
            skLineSegment(sketch, "E348", {"start": v(10.96, 11.76) * mm, "end": v(10.37, 10.6) * mm});
            skLineSegment(sketch, "E349", {"start": v(10.37, 10.6) * mm, "end": v(10.16, 9.83) * mm});
            skLineSegment(sketch, "E350", {"start": v(10.16, 9.83) * mm, "end": v(10.16, 9.36) * mm});
            skLineSegment(sketch, "E351", {"start": v(10.16, 9.36) * mm, "end": v(10.32, 9.02) * mm});
            skLineSegment(sketch, "E352", {"start": v(10.32, 9.02) * mm, "end": v(10.27, 7.57) * mm});
            skLineSegment(sketch, "E353", {"start": v(10.27, 7.57) * mm, "end": v(10.14, 7.34) * mm});
            skLineSegment(sketch, "E354", {"start": v(10.14, 7.34) * mm, "end": v(9.8, 7) * mm});
            skLineSegment(sketch, "E355", {"start": v(9.8, 7) * mm, "end": v(9.45, 6.86) * mm});
            skLineSegment(sketch, "E356", {"start": v(9.45, 6.86) * mm, "end": v(9.2, 6.73) * mm});
            skLineSegment(sketch, "E357", {"start": v(9.2, 6.73) * mm, "end": v(8.37, 6.76) * mm});
            skLineSegment(sketch, "E358", {"start": v(8.37, 6.76) * mm, "end": v(7.54, 7.05) * mm});
            skLineSegment(sketch, "E359", {"start": v(7.54, 7.05) * mm, "end": v(7.06, 7.2) * mm});
            skLineSegment(sketch, "E360", {"start": v(7.06, 7.2) * mm, "end": v(6.72, 7.3) * mm});
            skLineSegment(sketch, "E361", {"start": v(6.72, 7.3) * mm, "end": v(5.36, 7.3) * mm});
            skLineSegment(sketch, "E362", {"start": v(5.36, 7.3) * mm, "end": v(5.26, 7.27) * mm});
            skLineSegment(sketch, "E363", {"start": v(5.26, 7.27) * mm, "end": v(4.71, 7.29) * mm});
            skLineSegment(sketch, "E364", {"start": v(4.71, 7.29) * mm, "end": v(4.65, 7.08) * mm});
            skLineSegment(sketch, "E365", {"start": v(4.65, 7.08) * mm, "end": v(4.46, 6.97) * mm});
            skLineSegment(sketch, "E366", {"start": v(4.46, 6.97) * mm, "end": v(4.41, 6.8) * mm});
            skLineSegment(sketch, "E367", {"start": v(4.41, 6.8) * mm, "end": v(3.98, 6.35) * mm});
            skLineSegment(sketch, "E368", {"start": v(3.98, 6.35) * mm, "end": v(3.85, 5.87) * mm});
            skLineSegment(sketch, "E369", {"start": v(3.85, 5.87) * mm, "end": v(3.64, 5.34) * mm});
            skLineSegment(sketch, "E370", {"start": v(3.64, 5.34) * mm, "end": v(3.36, 4.79) * mm});
            skLineSegment(sketch, "E371", {"start": v(3.36, 4.79) * mm, "end": v(2.98, 4.21) * mm});
            skLineSegment(sketch, "E372", {"start": v(2.98, 4.21) * mm, "end": v(2.71, 3.9) * mm});
            skLineSegment(sketch, "E373", {"start": v(2.71, 3.9) * mm, "end": v(2.72, 3.74) * mm});
            skLineSegment(sketch, "E374", {"start": v(2.72, 3.74) * mm, "end": v(2.76, 3.27) * mm});
            skLineSegment(sketch, "E375", {"start": v(2.76, 3.27) * mm, "end": v(3.3, 3.24) * mm});
            skLineSegment(sketch, "E376", {"start": v(3.3, 3.24) * mm, "end": v(3.9, 2.94) * mm});
            skLineSegment(sketch, "E377", {"start": v(3.9, 2.94) * mm, "end": v(4.48, 2.55) * mm});
            skLineSegment(sketch, "E378", {"start": v(4.48, 2.55) * mm, "end": v(4.97, 2.18) * mm});
            skLineSegment(sketch, "E379", {"start": v(4.97, 2.18) * mm, "end": v(5.45, 1.8) * mm});
            skLineSegment(sketch, "E380", {"start": v(5.45, 1.8) * mm, "end": v(5.73, 1.53) * mm});
            skLineSegment(sketch, "E381", {"start": v(5.73, 1.53) * mm, "end": v(6.24, 1.2) * mm});
            skLineSegment(sketch, "E382", {"start": v(6.24, 1.2) * mm, "end": v(6.94, 1.16) * mm});
            skLineSegment(sketch, "E383", {"start": v(6.94, 1.16) * mm, "end": v(7.64, 1.35) * mm});
            skLineSegment(sketch, "E384", {"start": v(7.64, 1.35) * mm, "end": v(8.17, 1.48) * mm});
            skLineSegment(sketch, "E385", {"start": v(8.17, 1.48) * mm, "end": v(8.63, 1.54) * mm});
            skLineSegment(sketch, "E386", {"start": v(8.63, 1.54) * mm, "end": v(9.05, 1.62) * mm});
            skLineSegment(sketch, "E387", {"start": v(9.05, 1.62) * mm, "end": v(9.7, 1.57) * mm});
            skLineSegment(sketch, "E388", {"start": v(9.7, 1.57) * mm, "end": v(10.12, 1.53) * mm});
            skLineSegment(sketch, "E389", {"start": v(10.12, 1.53) * mm, "end": v(10.57, 1.47) * mm});
            skLineSegment(sketch, "E390", {"start": v(10.57, 1.47) * mm, "end": v(11.1, 1.36) * mm});
            skLineSegment(sketch, "E391", {"start": v(11.1, 1.36) * mm, "end": v(11.6, 1.22) * mm});
            skLineSegment(sketch, "E392", {"start": v(11.6, 1.22) * mm, "end": v(12.27, 1.05) * mm});
            skLineSegment(sketch, "E393", {"start": v(12.27, 1.05) * mm, "end": v(12.75, 0.96) * mm});
            skLineSegment(sketch, "E394", {"start": v(12.75, 0.96) * mm, "end": v(12.99, 0.87) * mm});
            skLineSegment(sketch, "E395", {"start": v(12.99, 0.87) * mm, "end": v(13.97, 0.9) * mm});
            skLineSegment(sketch, "E396", {"start": v(20.35, 42.08) * mm, "end": v(18.62, 42.08) * mm});
            skLineSegment(sketch, "E397", {"start": v(18.62, 42.08) * mm, "end": v(18.45, 42.02) * mm});
            skLineSegment(sketch, "E398", {"start": v(18.45, 42.02) * mm, "end": v(18.3, 41.94) * mm});
            skLineSegment(sketch, "E399", {"start": v(18.3, 41.94) * mm, "end": v(18.16, 41.88) * mm});
            skLineSegment(sketch, "E400", {"start": v(18.16, 41.88) * mm, "end": v(18.06, 41.73) * mm});
            skLineSegment(sketch, "E401", {"start": v(18.06, 41.73) * mm, "end": v(18.04, 41.65) * mm});
            skLineSegment(sketch, "E402", {"start": v(18.04, 41.65) * mm, "end": v(18.04, 40.79) * mm});
            skLineSegment(sketch, "E403", {"start": v(18.04, 40.79) * mm, "end": v(18.26, 40.79) * mm});
            skLineSegment(sketch, "E404", {"start": v(18.26, 40.79) * mm, "end": v(18.46, 40.88) * mm});
            skLineSegment(sketch, "E405", {"start": v(18.46, 40.88) * mm, "end": v(18.77, 40.95) * mm});
            skLineSegment(sketch, "E406", {"start": v(18.77, 40.95) * mm, "end": v(19.02, 41.03) * mm});
            skLineSegment(sketch, "E407", {"start": v(19.02, 41.03) * mm, "end": v(19.24, 41.13) * mm});
            skLineSegment(sketch, "E408", {"start": v(19.24, 41.13) * mm, "end": v(19.48, 41.22) * mm});
            skLineSegment(sketch, "E409", {"start": v(19.48, 41.22) * mm, "end": v(19.7, 41.32) * mm});
            skLineSegment(sketch, "E410", {"start": v(19.7, 41.32) * mm, "end": v(19.95, 41.48) * mm});
            skLineSegment(sketch, "E411", {"start": v(19.95, 41.48) * mm, "end": v(20.11, 41.63) * mm});
            skLineSegment(sketch, "E412", {"start": v(20.11, 41.63) * mm, "end": v(20.27, 41.75) * mm});
            skLineSegment(sketch, "E413", {"start": v(20.27, 41.75) * mm, "end": v(20.4, 41.88) * mm});
            skLineSegment(sketch, "E414", {"start": v(20.4, 41.88) * mm, "end": v(20.4, 42.09) * mm});
            skLineSegment(sketch, "E415", {"start": v(20.4, 42.09) * mm, "end": v(20.35, 42.08) * mm});
            skLineSegment(sketch, "E416", {"start": v(30.96, 32.95) * mm, "end": v(29.3, 27.47) * mm});
            skLineSegment(sketch, "E417", {"start": v(29.3, 27.47) * mm, "end": v(28.1, 27.7) * mm});
            skLineSegment(sketch, "E418", {"start": v(28.1, 27.7) * mm, "end": v(27.07, 23.57) * mm});
            skLineSegment(sketch, "E419", {"start": v(27.07, 23.57) * mm, "end": v(27.1, 23.4) * mm});
            skLineSegment(sketch, "E420", {"start": v(27.1, 23.4) * mm, "end": v(27.56, 22.56) * mm});
            skLineSegment(sketch, "E421", {"start": v(27.56, 22.56) * mm, "end": v(29.45, 19.62) * mm});
            skLineSegment(sketch, "E422", {"start": v(29.45, 19.62) * mm, "end": v(30.22, 19.12) * mm});
            skLineSegment(sketch, "E423", {"start": v(30.22, 19.12) * mm, "end": v(30.76, 18.85) * mm});
            skLineSegment(sketch, "E424", {"start": v(30.76, 18.85) * mm, "end": v(31.56, 18.85) * mm});
            skLineSegment(sketch, "E425", {"start": v(31.56, 18.85) * mm, "end": v(32.56, 18.93) * mm});
            skLineSegment(sketch, "E426", {"start": v(32.56, 18.93) * mm, "end": v(33.22, 19.2) * mm});
            skLineSegment(sketch, "E427", {"start": v(33.22, 19.2) * mm, "end": v(33.8, 19.56) * mm});
            skLineSegment(sketch, "E428", {"start": v(33.8, 19.56) * mm, "end": v(34.18, 19.9) * mm});
            skLineSegment(sketch, "E429", {"start": v(34.18, 19.9) * mm, "end": v(34.52, 20.44) * mm});
            skLineSegment(sketch, "E430", {"start": v(34.52, 20.44) * mm, "end": v(34.75, 20.93) * mm});
            skLineSegment(sketch, "E431", {"start": v(34.75, 20.93) * mm, "end": v(34.8, 21.19) * mm});
            skLineSegment(sketch, "E432", {"start": v(34.8, 21.19) * mm, "end": v(34.8, 23.04) * mm});
            skLineSegment(sketch, "E433", {"start": v(34.8, 23.04) * mm, "end": v(34.57, 23.85) * mm});
            skLineSegment(sketch, "E434", {"start": v(34.57, 23.85) * mm, "end": v(34.3, 24.83) * mm});
            skLineSegment(sketch, "E435", {"start": v(34.3, 24.83) * mm, "end": v(34, 26) * mm});
            skLineSegment(sketch, "E436", {"start": v(34, 26) * mm, "end": v(33.48, 27.37) * mm});
            skLineSegment(sketch, "E437", {"start": v(33.48, 27.37) * mm, "end": v(32.89, 28.98) * mm});
            skLineSegment(sketch, "E438", {"start": v(32.89, 28.98) * mm, "end": v(32.22, 30.67) * mm});
            skLineSegment(sketch, "E439", {"start": v(32.22, 30.67) * mm, "end": v(31.67, 31.81) * mm});
            skLineSegment(sketch, "E440", {"start": v(31.67, 31.81) * mm, "end": v(30.96, 32.95) * mm});
            skSolve(sketch);
        }
        {
            var Q0;
            Q0 = qSketchRegion(id + "F0", true);
            extrude(context, id + "F1", {"entities" : qUnion([Q0]), "depth" : 2 * mm, "offsetDistance" : 25 * mm});
        }
        {
            var Q0;
            Q0=qCreatedBy(makeId("Top.planeOp"),FACE);
            var sketch = newSketch(context, id + "F2", { "sketchPlane" : qUnion([Q0])});
            skText(sketch, "E441", { "text": "SAM", "fontName": "OpenSans-Bold.ttf"});
            const initialGuessF2  = {"E441": [0.00923, -0.0098, 1, 0, 0.00713]};
            skSetInitialGuess(sketch, initialGuessF2);
            skSolve(sketch);
        }
        {
            var Q0;
            Q0=makeQuery(id+"F2.imprint","IMPRINT",FACE,{"disambiguationData":[TD([[makeQuery(id+"F2.imprint","IMPRINT",EDGE,{"derivedFrom":sQuery(id+"F2.wireOp",EDGE,"E441.sketch_text.stroke-0")}),-1.0]])]});
            var Q1;
            Q1=makeQuery(id+"F2.imprint","IMPRINT",FACE,{"disambiguationData":[TD([[makeQuery(id+"F2.imprint","IMPRINT",EDGE,{"derivedFrom":sQuery(id+"F2.wireOp",EDGE,"E441.sketch_text.stroke-28")}),-1.0]])]});
            var Q2;
            Q2=makeQuery(id+"F2.imprint","IMPRINT",FACE,{"disambiguationData":[TD([[makeQuery(id+"F2.imprint","IMPRINT",EDGE,{"derivedFrom":sQuery(id+"F2.wireOp",EDGE,"E441.sketch_text.stroke-40")}),-1.0]])]});
            extrude(context, id + "F3", {"entities" : qUnion([Q0, Q1, Q2]), "depth" : 2 * mm, "offsetDistance" : 25 * mm});
        }
    });
